# Revit family: EL_Elektra_S_v2
name_source: partatom
category: Osvětlovací tělesa
units: mm (PartAtom-declared; Revit-internal decimal feet)

## family parameters
Bod výpočtu místnosti = Ne
Kóta kruhové spojky = Použít průměr
Název OmniClass = Lighting
Ořezat dutým tvarem při načtení = Ne
Sdílené = Ne
Typ součásti = Normální
Vždy vertikální = Ano
Zachovat orientaci poznámky = Ne
Založené na pracovní rovině = Ne
Zdroj světla = Ano
Číslo OmniClass = 23.80.70.00

## types (65) — shared parameters
Barevný filtr = 16777215
Bodové – úhel paprsku = 30.00°
CE Conformity = CE Mark
Certification = ENEC, ENEC+, EMC, Zhaga D4i, IDA
Control Gear = LED Driver
Diffuser Material  = Flat glass
Délka symbolu zdroje světla = 3048 mm  [stored 10 ft]
EL_Voltage = AC 220V - 240V / 50-60Hz
Housing Height = 97 mm  [stored 0.318241 ft]
Housing Length = 570 mm  [stored 1.87008 ft]
Housing Width = 280 mm  [stored 0.918635 ft]
IK = IK 09 / IK10
IP = IP66
Lampa = LED
Life Time = 120 000 h
Luminaire Material = Kov
Luminaire Type = ELEKTRA S
Model = ELEKTRA S
Popis = Street luminaire
Posunu barevné teploty při stmívání lampy = <Žádné>
Terminal Block Poles = 2, 3, 5
URL Luminaire = https://www.el-lumen.cz
URL Manufacturer = https://www.el-lumen.cz
Voltage  = AC 220V - 240V / 50-60Hz
Výchozí výška = 1500 mm  [stored 4.92126 ft]
Výrobce = ELEKTRO-LUMEN, s. r. o.
Weight = 4.8
Úhel bodového pole = 90.00°
Úhel náklonu = 90.00°

## per-type parameters (varying)
| type | CCT | CRI | Luminous Flux of LED | Luminous Flux of Luminaire | Optic | Optical Efficacy | Power |
| ELEKTRA S  Mxx 11k0 740 | 4000 | 70 | 11000 lm | 9633 lm | M03 | 87.57 | 65 W |
| ELEKTRA S  Mxx 10k0 740 | 4000 | 70 | 10000 lm | 8757 lm | M03 | 87.57 | 58 W |
| ELEKTRA S  Mxx 9k0 740 | 4000 | 70 | 9000 lm | 7881 lm | M03 | 87.57 | 55 W |
| ELEKTRA S  Mxx 8k0 740 | 4000 | 70 | 8000 lm | 7006 lm | M03 | 87.57 | 48 W |
| ELEKTRA S  Mxx 7k0 740 | 4000 | 70 | 7000 lm | 6130 lm | M03 | 87.57 | 41 W |
| ELEKTRA S  Mxx 6k0 740 | 4000 | 70 | 6000 lm | 5254 lm | M03 | 87.57 | 37 W |
| ELEKTRA S  Mxx 5k0 740 | 4000 | 70 | 5000 lm | 4379 lm | M03 | 87.57 | 31 W |
| ELEKTRA S  Mxx 4k0 740 | 4000 | 70 | 4000 lm | 3503 lm | M03 | 87.57 | 24 W |
| ELEKTRA S  Mxx 3k5 740 | 4000 | 70 | 3500 lm | 3065 lm | M03 | 87.57 | 21 W |
| ELEKTRA S  Mxx 3k0 740 | 4000 | 70 | 3000 lm | 2627 lm | M03 | 87.57 | 18 W |
| ELEKTRA S  Mxx 2k5 740 | 4000 | 70 | 2500 lm | 2189 lm | M03 | 87.57 | 15 W |
| ELEKTRA S  Mxx 2k0 740 | 4000 | 70 | 2000 lm | 1751 lm | M03 | 87.57 | 12 W |
| ELEKTRA S  Mxx 1k5 740 | 4000 | 70 | 1500 lm | 1314 lm | M03 | 87.57 | 9 W |
| ELEKTRA S  Mxx 1k0 740 | 4000 | 70 | 1000 lm | 876 lm | M03 | 87.57 | 7 W |
| ELEKTRA S  Mxx 11k0 730 | 3000 | 70 | 11000 lm | 9633 lm | M03 | 87.57 | 69 W |
| ELEKTRA S  Mxx 10k0 730 | 3000 | 70 | 10000 lm | 8757 lm | M03 | 87.57 | 61 W |
| ELEKTRA S  Mxx 9k0 730 | 3000 | 70 | 9000 lm | 7881 lm | M03 | 87.57 | 59 W |
| ELEKTRA S  Mxx 8k0 730 | 3000 | 70 | 8000 lm | 7006 lm | M03 | 87.57 | 51 W |
| ELEKTRA S  Mxx 7k0 730 | 3000 | 70 | 7000 lm | 6130 lm | M03 | 87.57 | 44 W |
| ELEKTRA S  Mxx 6k0 730 | 3000 | 70 | 6000 lm | 5254 lm | M03 | 87.57 | 40 W |
| ELEKTRA S  Mxx 5k0 730 | 3000 | 70 | 5000 lm | 4379 lm | M03 | 87.57 | 32 W |
| ELEKTRA S  Mxx 4k0 730 | 3000 | 70 | 4000 lm | 3503 lm | M03 | 87.57 | 25 W |
| ELEKTRA S  Mxx 3k5 730 | 3000 | 70 | 3500 lm | 3065 lm | M03 | 87.57 | 22 W |
| ELEKTRA S  Mxx 3k0 730 | 3000 | 70 | 3000 lm | 2627 lm | M03 | 87.57 | 18 W |
| ELEKTRA S  Mxx 2k5 730 | 3000 | 70 | 2500 lm | 2189 lm | M03 | 87.57 | 15 W |
| ELEKTRA S  Mxx 2k0 730 | 3000 | 70 | 2000 lm | 1751 lm | M03 | 87.57 | 12 W |
| ELEKTRA S  Mxx 1k5 730 | 3000 | 70 | 1500 lm | 1314 lm | M03 | 87.57 | 10 W |
| ELEKTRA S  Mxx 1k0 730 | 3000 | 70 | 1000 lm | 876 lm | M03 | 87.57 | 7 W |
| ELEKTRA S  Mxx 10k0 727 | 2700 | 70 | 10000 lm | 8757 lm | M03 | 87.57 | 65 W |
| ELEKTRA S  Mxx 9k0 727 | 2700 | 70 | 9000 lm | 7881 lm | M03 | 87.57 | 58 W |
| ELEKTRA S  Mxx 8k0 727 | 2700 | 70 | 8000 lm | 7006 lm | M03 | 87.57 | 54 W |
| ELEKTRA S  Mxx 7k0 727 | 2700 | 70 | 7000 lm | 6130 lm | M03 | 87.57 | 46 W |
| ELEKTRA S  Mxx 6k0 727 | 2700 | 70 | 6000 lm | 5254 lm | M03 | 87.57 | 43 W |
| ELEKTRA S  Mxx 5k0 727 | 2700 | 70 | 5000 lm | 4379 lm | M03 | 87.57 | 34 W |
| ELEKTRA S  Mxx 4k0 727 | 2700 | 70 | 4000 lm | 3503 lm | M03 | 87.57 | 27 W |
| ELEKTRA S  Mxx 3k5 727 | 2700 | 70 | 3500 lm | 3065 lm | M03 | 87.57 | 23 W |
| ELEKTRA S  Mxx 3k0 727 | 2700 | 70 | 3000 lm | 2627 lm | M03 | 87.57 | 20 W |
| ELEKTRA S  Mxx 2k5 727 | 2700 | 70 | 2500 lm | 2189 lm | M03 | 87.57 | 16 W |
| ELEKTRA S  Mxx 2k0 727 | 2700 | 70 | 2000 lm | 1751 lm | M03 | 87.57 | 13 W |
| ELEKTRA S  Mxx 1k5 727 | 2700 | 70 | 1500 lm | 1314 lm | M03 | 87.57 | 10 W |
| ELEKTRA S  Mxx 1k0 727 | 2700 | 70 | 1000 lm | 876 lm | M03 | 87.57 | 7 W |
| ELEKTRA S  Mxx 9k0 722 | 2200 | 70 | 9000 lm | 7881 lm | M03 | 87.57 | 67 W |
| ELEKTRA S  Mxx 8k0 722 | 2200 | 70 | 8000 lm | 7006 lm | M03 | 87.57 | 58 W |
| ELEKTRA S  Mxx 7k0 722 | 2200 | 70 | 7000 lm | 6130 lm | M03 | 87.57 | 54 W |
| ELEKTRA S  Mxx 6k0 722 | 2200 | 70 | 6000 lm | 5254 lm | M03 | 87.57 | 45 W |
| ELEKTRA S  Mxx 5k0 722 | 2200 | 70 | 5000 lm | 4379 lm | M03 | 87.57 | 40 W |
| ELEKTRA S  Mxx 4k0 722 | 2200 | 70 | 4000 lm | 3503 lm | M03 | 87.57 | 31 W |
| ELEKTRA S  Mxx 3k5 722 | 2200 | 70 | 3500 lm | 3065 lm | M03 | 87.57 | 26 W |
| ELEKTRA S  Mxx 3k0 722 | 2200 | 70 | 3000 lm | 2627 lm | M03 | 87.57 | 23 W |
| ELEKTRA S  Mxx 2k5 722 | 2200 | 70 | 2500 lm | 2189 lm | M03 | 87.57 | 18 W |
| ELEKTRA S  Mxx 2k0 722 | 2200 | 70 | 2000 lm | 1751 lm | M03 | 87.57 | 15 W |
| ELEKTRA S  Mxx 1k5 722 | 2200 | 70 | 1500 lm | 1314 lm | M03 | 87.57 | 12 W |
| ELEKTRA S  Mxx 1k0 722 | 2200 | 70 | 1000 lm | 876 lm | M03 | 87.57 | 8 W |
| ELEKTRA S  Lxx 9k0 AMB | 1850 | 50 | 9000 lm | 8001 lm | L03 | 88.9 | 61 W |
| ELEKTRA S  Lxx 8k0 AMB | 1850 | 50 | 8000 lm | 7112 lm | L03 | 88.9 | 53 W |
| ELEKTRA S  Lxx 7k0 AMB | 1850 | 50 | 7000 lm | 6223 lm | L03 | 88.9 | 48 W |
| ELEKTRA S  Lxx 6k0 AMB | 1850 | 50 | 6000 lm | 5334 lm | L03 | 88.9 | 41 W |
| ELEKTRA S  Lxx 5k0 AMB | 1850 | 50 | 5000 lm | 4445 lm | L03 | 88.9 | 36 W |
| ELEKTRA S  Lxx 4k0 AMB | 1850 | 50 | 4000 lm | 3556 lm | L03 | 88.9 | 28 W |
| ELEKTRA S  Lxx 3k5 AMB | 1850 | 50 | 3500 lm | 3112 lm | L03 | 88.9 | 25 W |
| ELEKTRA S  Lxx 3k0 AMB | 1850 | 50 | 3000 lm | 2667 lm | L03 | 88.9 | 21 W |
| ELEKTRA S  Lxx 2k5 AMB | 1850 | 50 | 2500 lm | 2223 lm | L03 | 88.9 | 18 W |
| ELEKTRA S  Lxx 2k0 AMB | 1850 | 50 | 2000 lm | 1778 lm | L03 | 88.9 | 14 W |
| ELEKTRA S  Lxx 1k5 AMB | 1850 | 50 | 1500 lm | 1334 lm | L03 | 88.9 | 11 W |
| ELEKTRA S  Lxx 1k0 AMB | 1850 | 50 | 1000 lm | 889 lm | L03 | 88.9 | 8 W |

note: column(s) folded — value = type name in every type: Luminaire Model

note: [stored X ft] marks values corroborated as IEEE doubles in the binary element streams (Revit-internal decimal feet)
